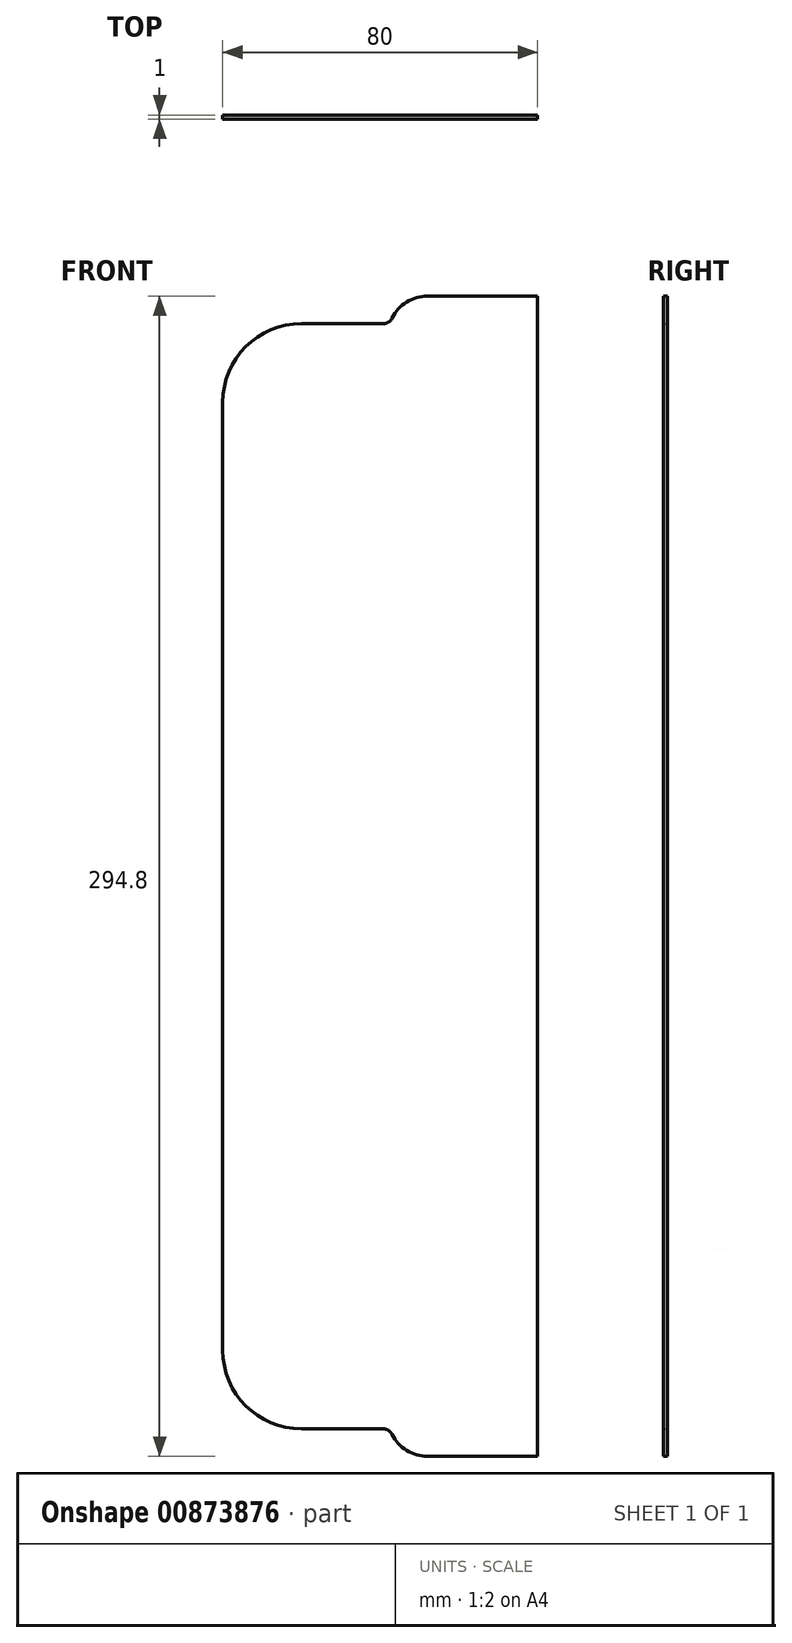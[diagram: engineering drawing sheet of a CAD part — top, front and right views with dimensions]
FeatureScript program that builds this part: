
annotation { "Feature Type Name" : "Feature", "Feature Type Description" : "" }
export const myFeature = defineFeature(function(context is Context, id is Id, definition is map)
    precondition{}
    {
        {
            var Q0;
            Q0=qCreatedBy(makeId("Front.planeOp"),FACE);
            var sketch = newSketch(context, id + "F0", { "sketchPlane" : qUnion([Q0])});
            skLineSegment(sketch, "E0", {"start": v(0, 0) * mm, "end": v(0, 120.4) * mm});
            skLineSegment(sketch, "E1", {"start": v(20, 140.4) * mm, "end": v(40.78, 140.4) * mm});
            skPoint(sketch, "E2.visualSharp", {"position": v(0, 140.4) * mm});
            skArc(sketch, "E2.filletArc", {"start": v(20, 140.4) * mm, "mid": v(5.86, 134.54) * mm, "end": v(0, 120.4) * mm});
            skArc(sketch, "E3", {"start": v(52, 147.4) * mm, "mid": v(46.7, 145.89) * mm, "end": v(43.02, 141.8) * mm});
            skLineSegment(sketch, "E4", {"start": v(52, 147.4) * mm, "end": v(80, 147.4) * mm});
            skLineSegment(sketch, "E5", {"start": v(80, 147.4) * mm, "end": v(80, 0) * mm});
            skPoint(sketch, "E6.visualSharp", {"position": v(42.46, 140.4) * mm});
            skArc(sketch, "E6.filletArc", {"start": v(40.78, 140.4) * mm, "mid": v(42.1, 140.78) * mm, "end": v(43.02, 141.8) * mm});
            skArc(sketch, "E7.MirrorCS", {"start": v(40.78, -140.4) * mm, "mid": v(42.1, -140.78) * mm, "end": v(43.02, -141.8) * mm});
            skArc(sketch, "E8.MirrorCS", {"start": v(52, -147.4) * mm, "mid": v(46.7, -145.89) * mm, "end": v(43.02, -141.8) * mm});
            skLineSegment(sketch, "E9.MirrorCS", {"start": v(20, -140.4) * mm, "end": v(40.78, -140.4) * mm});
            skPoint(sketch, "E10.MirrorP", {"position": v(42.46, -140.4) * mm});
            skLineSegment(sketch, "E11.MirrorCS", {"start": v(0, 0) * mm, "end": v(0, -120.4) * mm});
            skLineSegment(sketch, "E12.MirrorCS", {"start": v(52, -147.4) * mm, "end": v(80, -147.4) * mm});
            skPoint(sketch, "E13.MirrorP", {"position": v(0, -140.4) * mm});
            skArc(sketch, "E14.MirrorCS", {"start": v(20, -140.4) * mm, "mid": v(5.86, -134.54) * mm, "end": v(0, -120.4) * mm});
            skLineSegment(sketch, "E15.MirrorCS", {"start": v(80, -147.4) * mm, "end": v(80, 0) * mm});
            skSolve(sketch);
        }
        {
            var Q0;
            Q0 = qSketchRegion(id + "F0", true);
            extrude(context, id + "F1", {"entities" : qUnion([Q0]), "depth" : 1 * mm, "offsetDistance" : 25 * mm});
        }
    });
